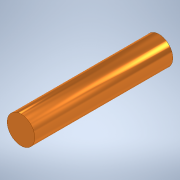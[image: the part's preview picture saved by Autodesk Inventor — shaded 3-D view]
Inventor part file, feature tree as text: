
AUTODESK INVENTOR PART (.ipt)
format: ipt  version: 2022 (Build 260153000, 153)  size: 97,792 bytes
history: native  units: in
note: dims shown in document units (in); Inventor stores cm internally (conversion verified against a paired STEP export)
features: extrude x1, sketch x1
ambient origin geometry x8: Origin, YZ Plane, XZ Plane, XY Plane, X Axis, Y Axis, Z Axis, Center Point
bodies: Solid1 (feature_tree)
feature tree (2):
  extrude  "Extrusion1"  Depth=0.5in TaperAngle=0.0deg
  sketch  "Sketch1"  dims[d0=0.1in d1=0.5in d2=0.0in]
